# Revit family: ISI_IdealStandard_WCSeats_Dea_SeatAndCover
name_source: partatom
category: Plumbing Fixtures
revit_build: Autodesk Revit MEP 2012 (Build: 20110309_2315(x64)
units: mm (PartAtom-declared; Revit-internal decimal feet)

## types (3) — shared parameters
Accessories = www.idealspec.co.uk
AreaUnits = millimeters
Assembly Code = C1030200
AssetType = Fixed
Brand = Ideal Standard
ConnectionType = Plumbing
Default Elevation = 1219 mm
DurationUnit = year
ECA = No
ExpectedLife = 5
Help = www.idealspec.co.uk/contact-us.html
IfcExportAs = IfcSanitaryTerminalType
IfcExportType = WCSEAT
InstallationInstructions = www.idealspec.co.uk/resources.html
LinearUnits = millimeters
ManufacturerURL = www.idealspec.co.uk
Material = Duroplast
NBSDescription = WC seats and covers
NBSReference = 45-35-70/391
Name = WCSeats_Dea-Seat&Cover-AllVariants_IdealStandard
NettWeight = 2 Kg
NominalDepth = 443 mm
NominalHeight = 42 mm
NominalLength = 443 mm
NominalWidth = 366 mm
ProductInformation = www.idealspec.co.uk/assets/datasheet/T329301
SeatColor = White
SeatHasCover = Yes
SeatMaterial = Plastic
SeatType = RingSeat
Shape = Ring
Space = Internal
SpareParts = www.fastpart-spares.co.uk
URL = www.idealspec.co.uk
Uniclass2 = Pr_40_20_93_95
Version = 2
VolumeUnits = Litres
WRAS = No
WarrantyDescription = Manufacturers Warranty
WarrantyDurationParts = 5
WarrantyDurationUnit = year
WaterEfficientProduct = No
zero-valued in all types: CWFU, Cost, HWFU, WFU

## per-type parameters (varying)
| type | BIMObjectName | Color | Description | Features | Finish | Model | ModelNumber | ModelReference | Size |
| T676601-Dea Seat and Cover-Standard Close (White Gloss) | ISI_IdealStandard_WCSeats_Dea-Seat&Cover_T676601 | White Gloss | Dea seat&cover | Standard close | White Gloss | T676601 | T676601 | Dea seat&cover | 366 x 443 x 41mm |
| T676701-Dea Seat and Cover-Slow Close (White Gloss) | ISI_IdealStandard_WCSeats_Dea-Seat&Cover_T676701 | White Gloss | Dea seat & cover slow close | Slow close | White Gloss | T676701 | T676701 | Dea seat & cover slow close | 366 x 443 x 41 mm |
| T676783-Dea Seat and Cover-Slow Close (White Matt) | ISI_IdealStandard_WCSeats_Dea-Seat&Cover_T676783 | White Matt | Dea seat & cover slow close | Slow close | White Matt | T676783 | T676783 | Dea seat & cover slow close | 366 x 443 x 41 mm |

## geometry (parser evidence)
native form markers: Sweep x3
no freeform markers — native parametric forms only
